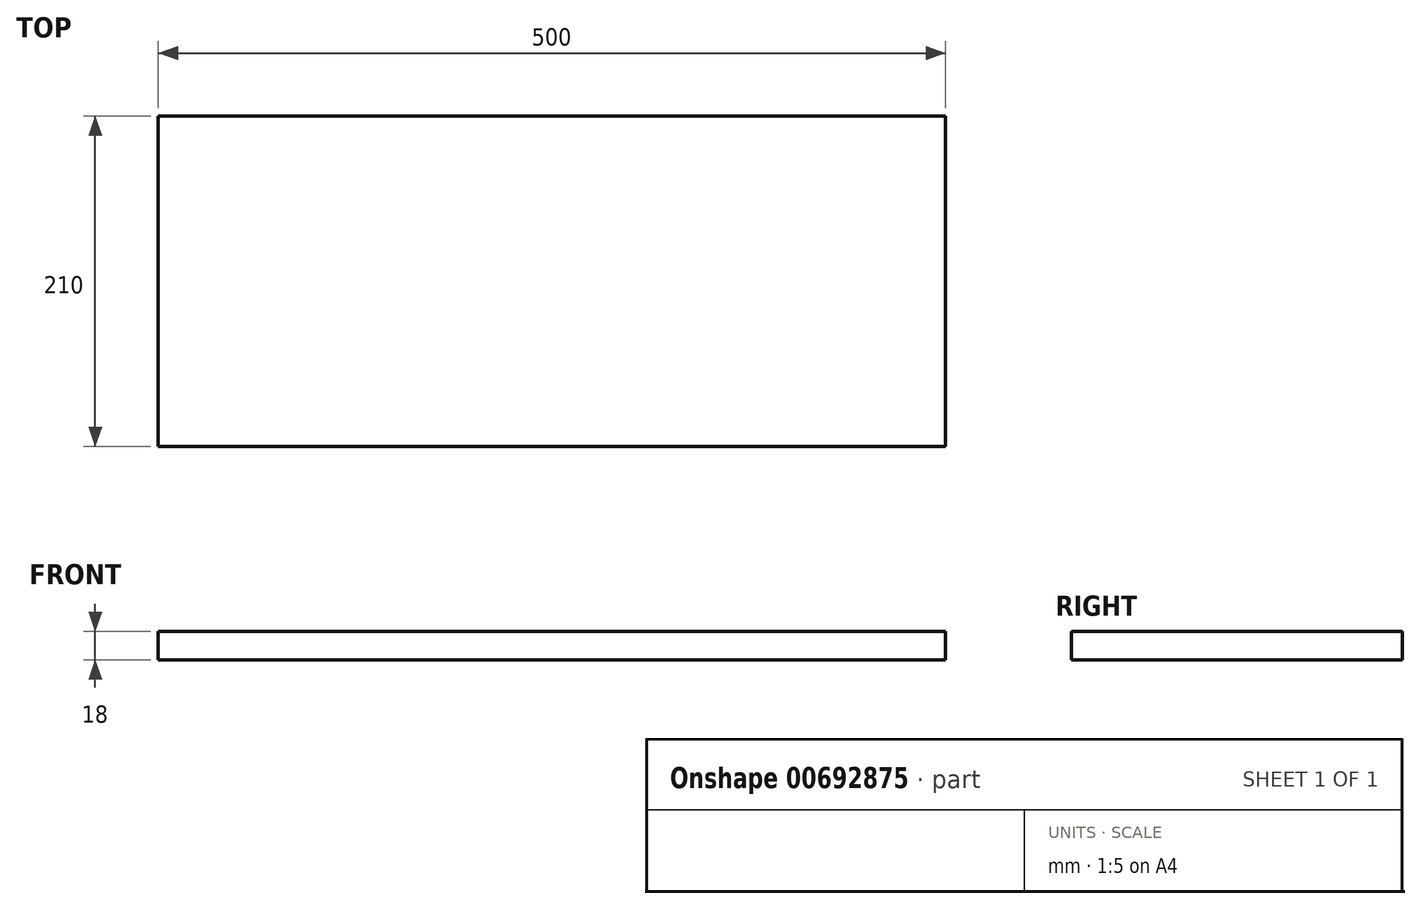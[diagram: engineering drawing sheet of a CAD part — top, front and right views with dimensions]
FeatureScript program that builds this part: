
annotation { "Feature Type Name" : "Feature", "Feature Type Description" : "" }
export const myFeature = defineFeature(function(context is Context, id is Id, definition is map)
    precondition{}
    {
        {
            var Q0;
            Q0=qCreatedBy(makeId("Top.planeOp"),FACE);
            var sketch = newSketch(context, id + "F0", { "sketchPlane" : qUnion([Q0])});
            skLineSegment(sketch, "E0.bottom", {"start": v(250, 105) * mm, "end": v(-250, 105) * mm});
            skLineSegment(sketch, "E0.top", {"start": v(250, -105) * mm, "end": v(-250, -105) * mm});
            skLineSegment(sketch, "E0.left", {"start": v(250, 105) * mm, "end": v(250, -105) * mm});
            skLineSegment(sketch, "E0.right", {"start": v(-250, 105) * mm, "end": v(-250, -105) * mm});
            skPoint(sketch, "E0.middle", {"position": v(0, 0) * mm});
            skSolve(sketch);
        }
        {
            var Q0;
            Q0 = qSketchRegion(id + "F0", true);
            extrude(context, id + "F1", {"entities" : qUnion([Q0]), "depth" : 18 * mm, "offsetDistance" : 25 * mm});
        }
    });
